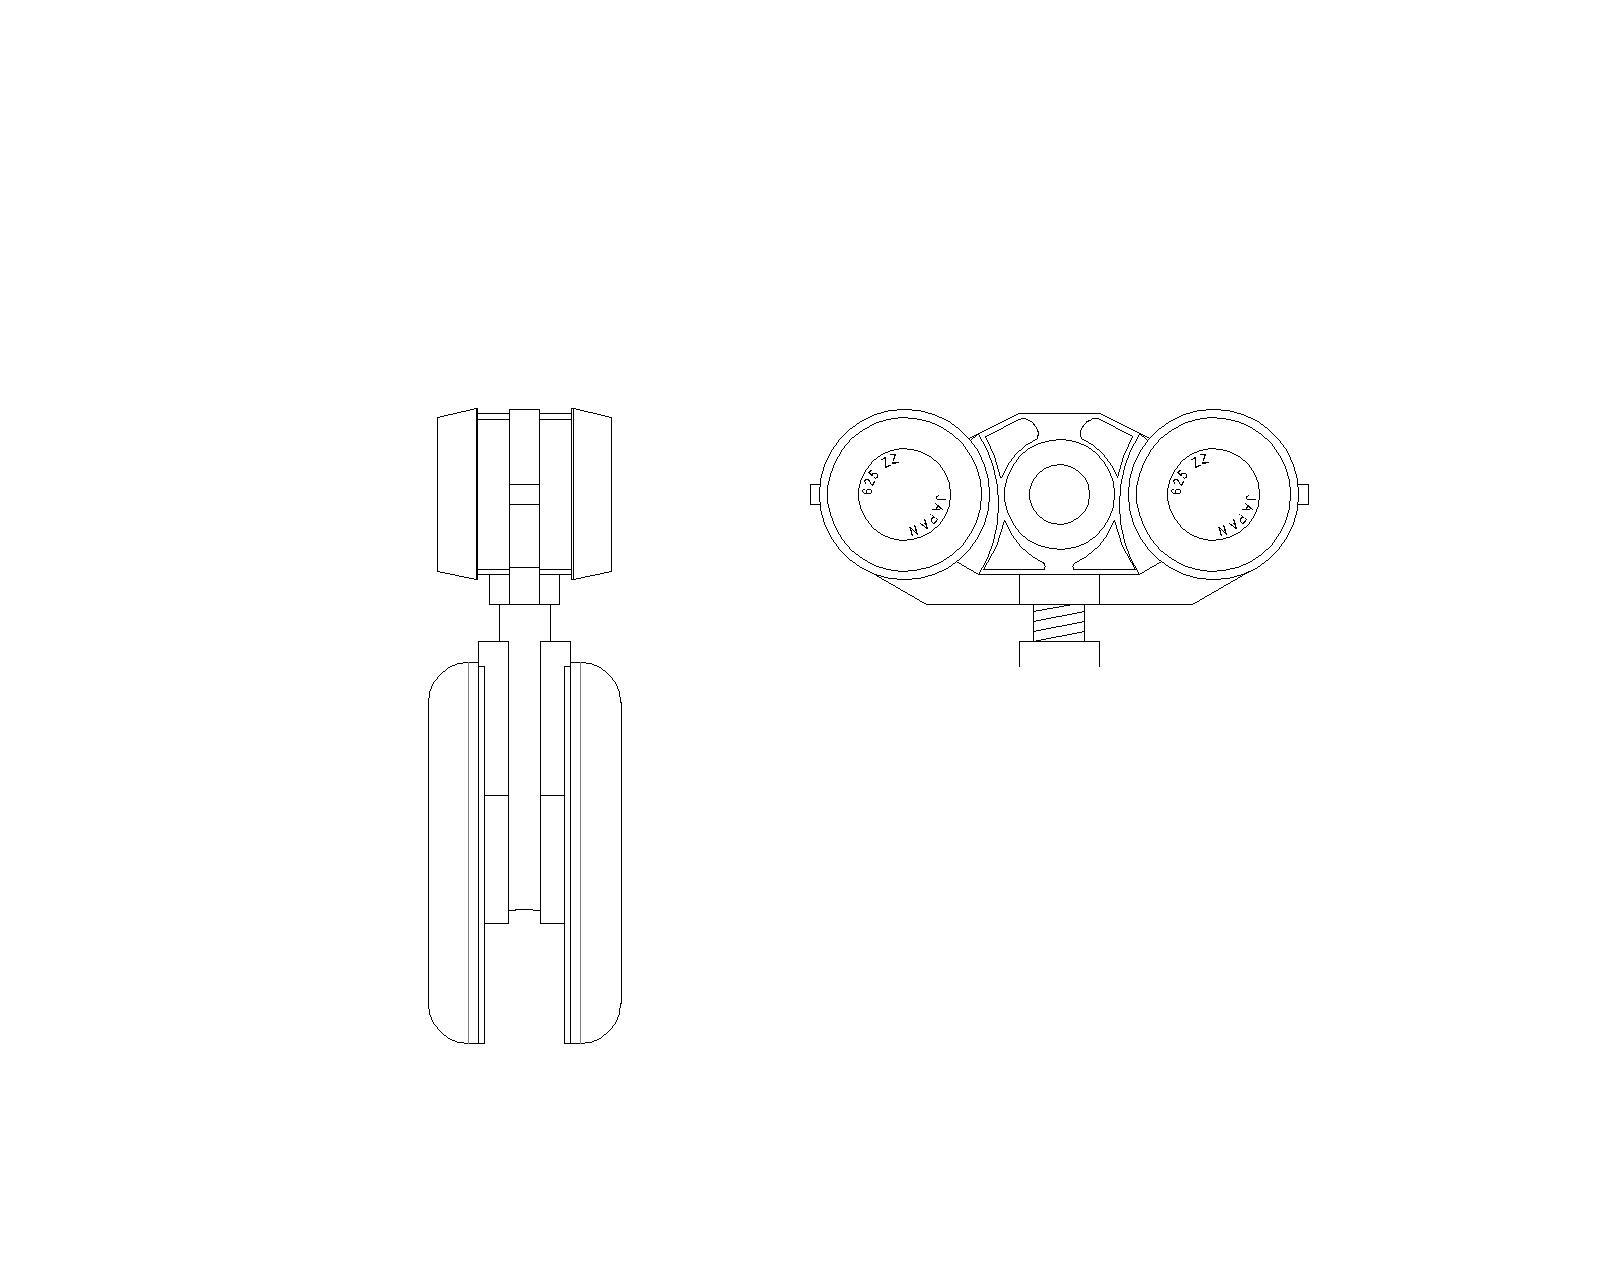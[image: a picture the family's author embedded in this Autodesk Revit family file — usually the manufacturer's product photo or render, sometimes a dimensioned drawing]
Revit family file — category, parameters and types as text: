
# Revit family: PRL_Tiffany_Series
name_source: partatom
category: Puertas
units: mm (PartAtom-declared; Revit-internal decimal feet)

## family parameters
Anfitrión = Muro
Compartido = No
Corte con vacíos al cargar = No
Número OmniClass = 23.30.10.00
Punto de cálculo de habitación = No
Siempre vertical = Sí
Título OmniClass = Doors

## types (1)
- PRL_Tiffany_Series
    Altura = 7' - 10 1/2"
    Anchura = 11' - 0"
    Cierre de muro = Por anfitrión
    Construcción analítica = <Ninguno>
    Definir propiedades térmicas por = Tipo esquemático
    Frame Projection Ext. = 0' - 1"
    Frame Projection Int. = 0' - 1"
    Frame Width = 0' - 3"
    Función = Interior
    XCFX = 01 Fascia Mount X : Fascia Mount X
    XCFXX = 03 Fascia Mount XX : Fascia Mount XX
    XCWOOXXOO = 09 Wall Mount OOXXOO : Wall Mount OOXXOO
    XCWOX = 06 Wall Mount OX : Wall Mount OX
    XCWOXO = 07 Wall Mount OXO : Wall Mount OXO
    XCWOXXO = 08 Wall Mount OXXO : Wall Mount OXXO
    XCWX = 02 Wall Mount X (Pocket system) : Wall Mount X (Pocket system)
    XCWXX = 04 Wall Mount XX (Pocket system) : Wall Mount XX (Pocket system)
    XG12 = 1/2"
    XG38 = 3/8"
    XR2 = 2 Rolles (200 lb)
    XR3 = 3 Rolles (275 lb)

## geometry (parser evidence)
native form markers: Sweep x105
no freeform markers — native parametric forms only
